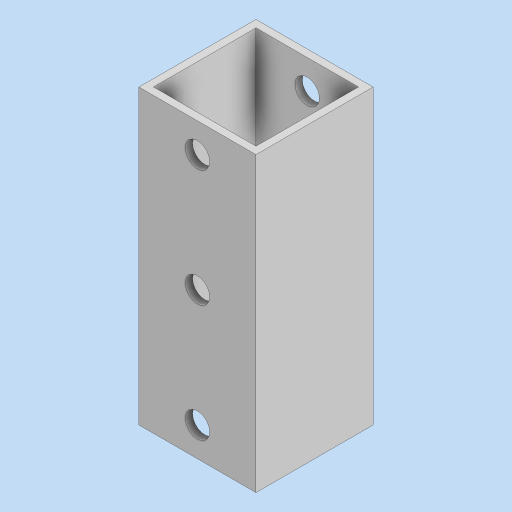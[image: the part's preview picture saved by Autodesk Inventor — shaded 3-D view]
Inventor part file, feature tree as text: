
AUTODESK INVENTOR PART (.ipt)
format: ipt  version: 2024 (Build 280153000, 153)  size: 125,952 bytes
history: native  units: in
note: dims shown in document units (in); Inventor stores cm internally (conversion verified against a paired STEP export)
features: extrude x2, sketch x2
ambient origin geometry x8: Origin, YZ Plane, XZ Plane, XY Plane, X Axis, Y Axis, Z Axis, Center Point
bodies: Solid1 (feature_tree)
feature tree (4):
  extrude  "Extrusion1"  Depth=1.0in
  extrude  "Extrusion2"  Depth=0.0625in
  sketch  "Sketch1"  dims[d0=1.0in d1=1.0in]
  sketch  "Sketch2"  dims[d2=0.0625in d3=0.0625in d4=0.0625in d5=0.0625in d6=2.5in d7=0.0in d8=0.2087in d9=1.0in d10=1.0in d11=0.0in d12=0.0in]
